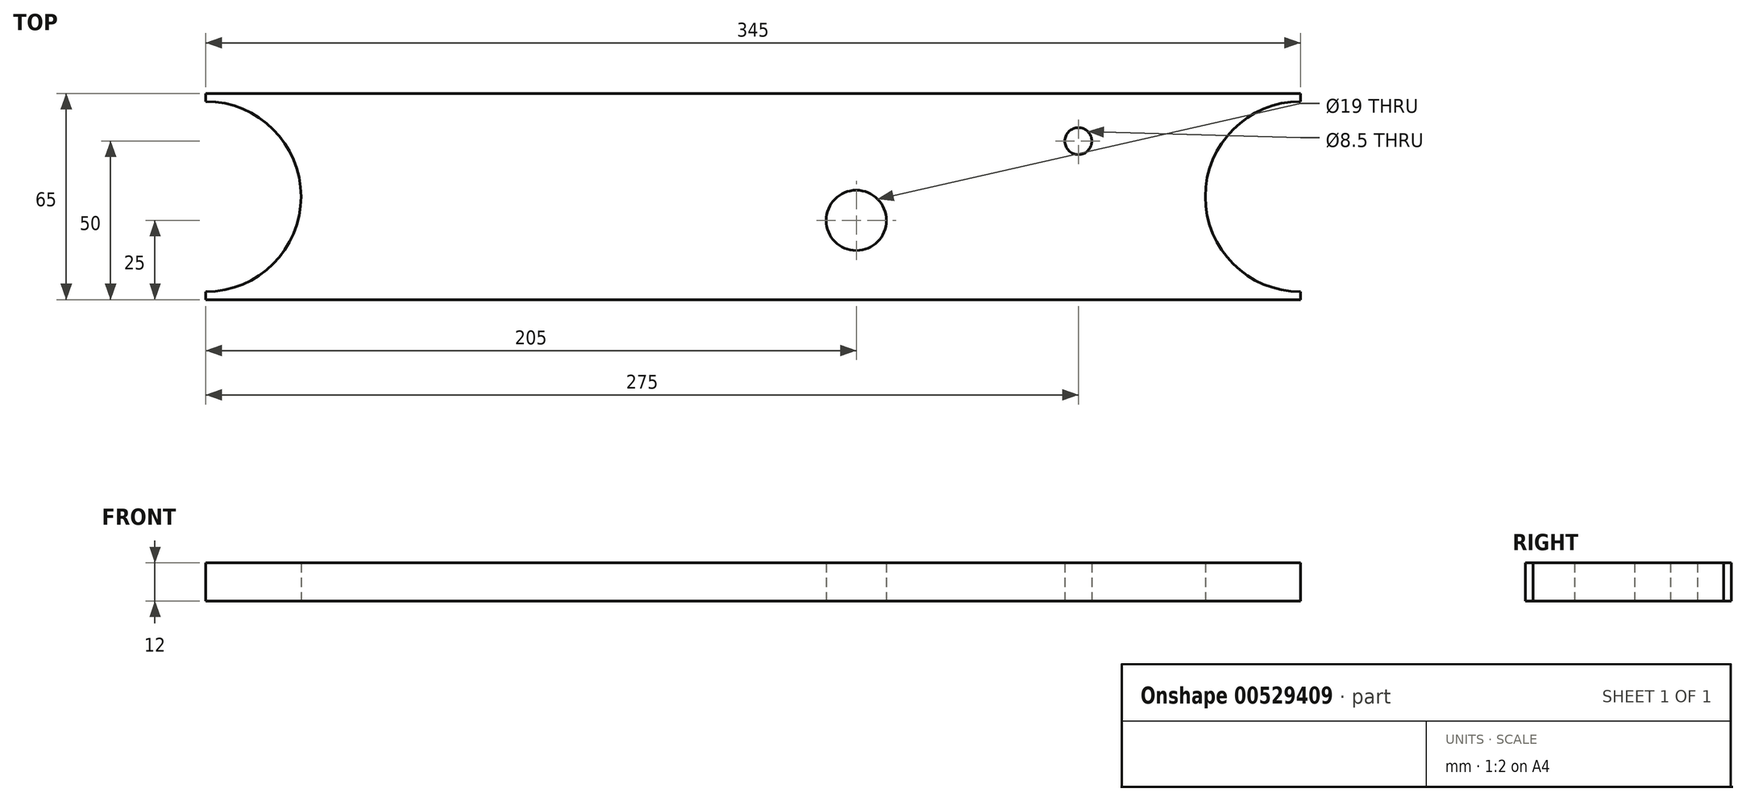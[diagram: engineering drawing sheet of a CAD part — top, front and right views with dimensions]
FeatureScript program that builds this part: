
annotation { "Feature Type Name" : "Feature", "Feature Type Description" : "" }
export const myFeature = defineFeature(function(context is Context, id is Id, definition is map)
    precondition{}
    {
        {
            var Q0;
            Q0=qCreatedBy(makeId("Top.planeOp"),FACE);
            var sketch = newSketch(context, id + "F0", { "sketchPlane" : qUnion([Q0])});
            skLineSegment(sketch, "E0.bottom", {"start": v(-172.5, 32.5) * mm, "end": v(172.5, 32.5) * mm});
            skLineSegment(sketch, "E0.top", {"start": v(-172.5, -32.5) * mm, "end": v(172.5, -32.5) * mm});
            skLineSegment(sketch, "E0.left", {"start": v(-172.5, 32.5) * mm, "end": v(-172.5, -32.5) * mm});
            skLineSegment(sketch, "E0.right", {"start": v(172.5, 32.5) * mm, "end": v(172.5, -32.5) * mm});
            skPoint(sketch, "E0.middle", {"position": v(0, 0) * mm});
            skLineSegment(sketch, "E1", {"start": v(-172.5, 0) * mm, "end": v(172.5, 0) * mm, "construction": true});
            skCircle(sketch, "E2", {"center": v(-172.5, 0) * mm, "radius": 30 * mm});
            skCircle(sketch, "E3", {"center": v(172.5, 0) * mm, "radius": 30 * mm});
            skLineSegment(sketch, "E4", {"start": v(32.5, 32.5) * mm, "end": v(32.5, -7.5) * mm, "construction": true});
            skLineSegment(sketch, "E5", {"start": v(102.5, 32.5) * mm, "end": v(102.5, 17.5) * mm, "construction": true});
            skCircle(sketch, "E6", {"center": v(32.5, -7.5) * mm, "radius": 9.5 * mm});
            skCircle(sketch, "E7", {"center": v(102.5, 17.5) * mm, "radius": 4.25 * mm});
            skSolve(sketch);
        }
        {
            var Q0;
            {var subQ4=sQuery(id+"F0.wireOp",EDGE,"E0.bottom");Q0=makeQuery(id+"F0.imprint","IMPRINT",FACE,{"disambiguationData":[TD([[makeQuery(id+"F0.imprint","IMPRINT",EDGE,{"derivedFrom":subQ4}),-1.0]])]});}
            extrude(context, id + "F1", {"entities" : qUnion([Q0]), "endBound" : BoundingType.SYMMETRIC, "depth" : 12 * mm, "offsetDistance" : 25 * mm});
        }
    });
